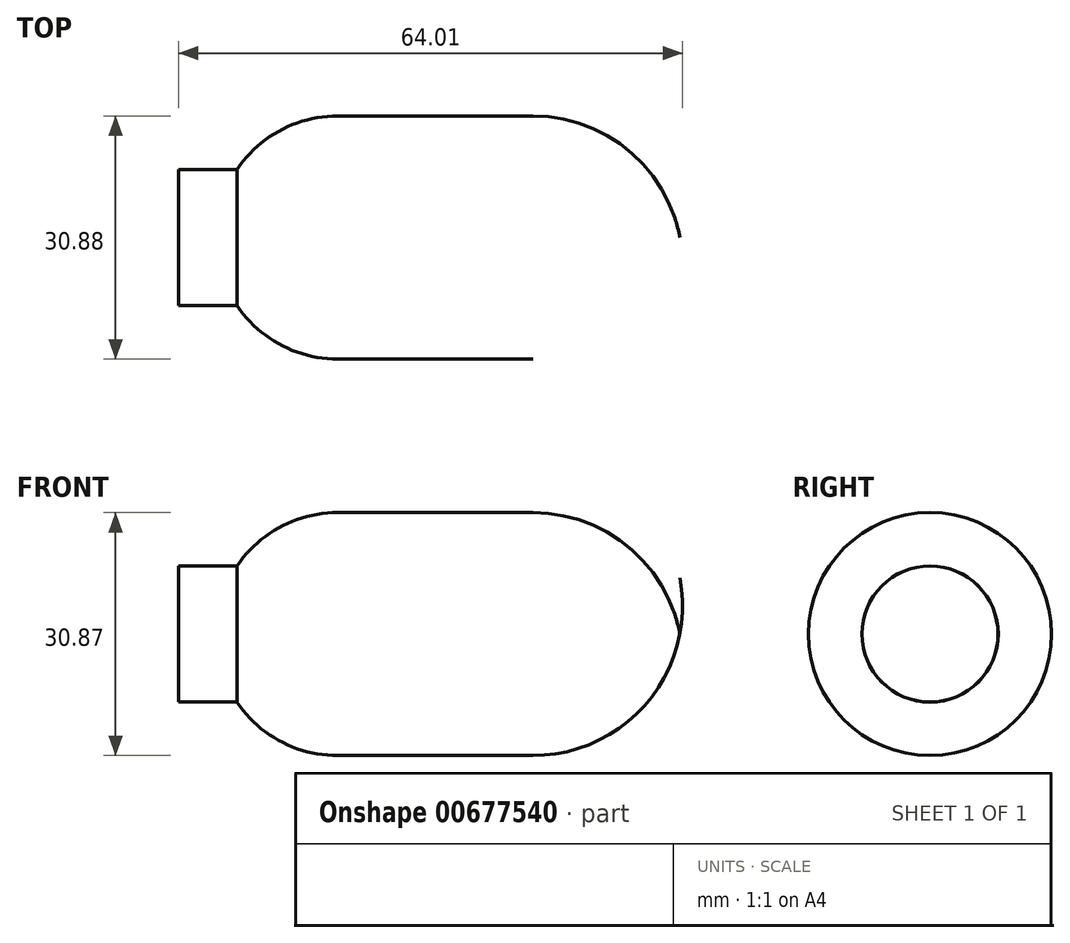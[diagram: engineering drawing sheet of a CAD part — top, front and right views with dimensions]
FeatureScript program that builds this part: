
annotation { "Feature Type Name" : "Feature", "Feature Type Description" : "" }
export const myFeature = defineFeature(function(context is Context, id is Id, definition is map)
    precondition{}
    {
        {
            var Q0;
            Q0=qCreatedBy(makeId("Front.planeOp"),FACE);
            var sketch = newSketch(context, id + "F0", { "sketchPlane" : qUnion([Q0])});
            skLineSegment(sketch, "E0", {"start": v(220.92, 25.5) * mm, "end": v(220.92, 16.87) * mm});
            skLineSegment(sketch, "E1", {"start": v(220.92, 16.87) * mm, "end": v(284.93, 16.87) * mm});
            skLineSegment(sketch, "E2", {"start": v(220.92, 25.5) * mm, "end": v(228.24, 25.5) * mm});
            skLineSegment(sketch, "E3", {"start": v(241.11, 32.3) * mm, "end": v(265.93, 32.3) * mm});
            skLineSegment(sketch, "E4", {"start": v(284.93, 16.87) * mm, "end": v(284.93, 13.3) * mm});
            skPoint(sketch, "E5.visualSharp", {"position": v(284.93, 32.3) * mm});
            skArc(sketch, "E5.filletArc", {"start": v(284.93, 13.3) * mm, "mid": v(279.36, 26.74) * mm, "end": v(265.93, 32.3) * mm});
            skPoint(sketch, "E6.visualSharp", {"position": v(228.28, 25.5) * mm});
            skArc(sketch, "E6.filletArc", {"start": v(228.24, 25.5) * mm, "mid": v(228.28, 25.51) * mm, "end": v(228.33, 25.53) * mm});
            skArc(sketch, "E7", {"start": v(241.11, 32.3) * mm, "mid": v(233.88, 30.5) * mm, "end": v(228.33, 25.53) * mm});
            skSolve(sketch);
        }
        {
            var Q0;
            {var subQ2=sQuery(id+"F0.wireOp",EDGE,"E0");Q0=makeQuery(id+"F0.imprint","IMPRINT",FACE,{"disambiguationData":[TD([[makeQuery(id+"F0.imprint","IMPRINT",EDGE,{"derivedFrom":subQ2}),1.0]])]});}
            var Q1;
            Q1=sQuery(id+"F0.wireOp",EDGE,"E1");
            revolve(context, id + "F1", {"entities" : qUnion([Q0]), "axis" : qUnion([Q1]), "revolveType" : RevolveType.FULL});
        }
    });
